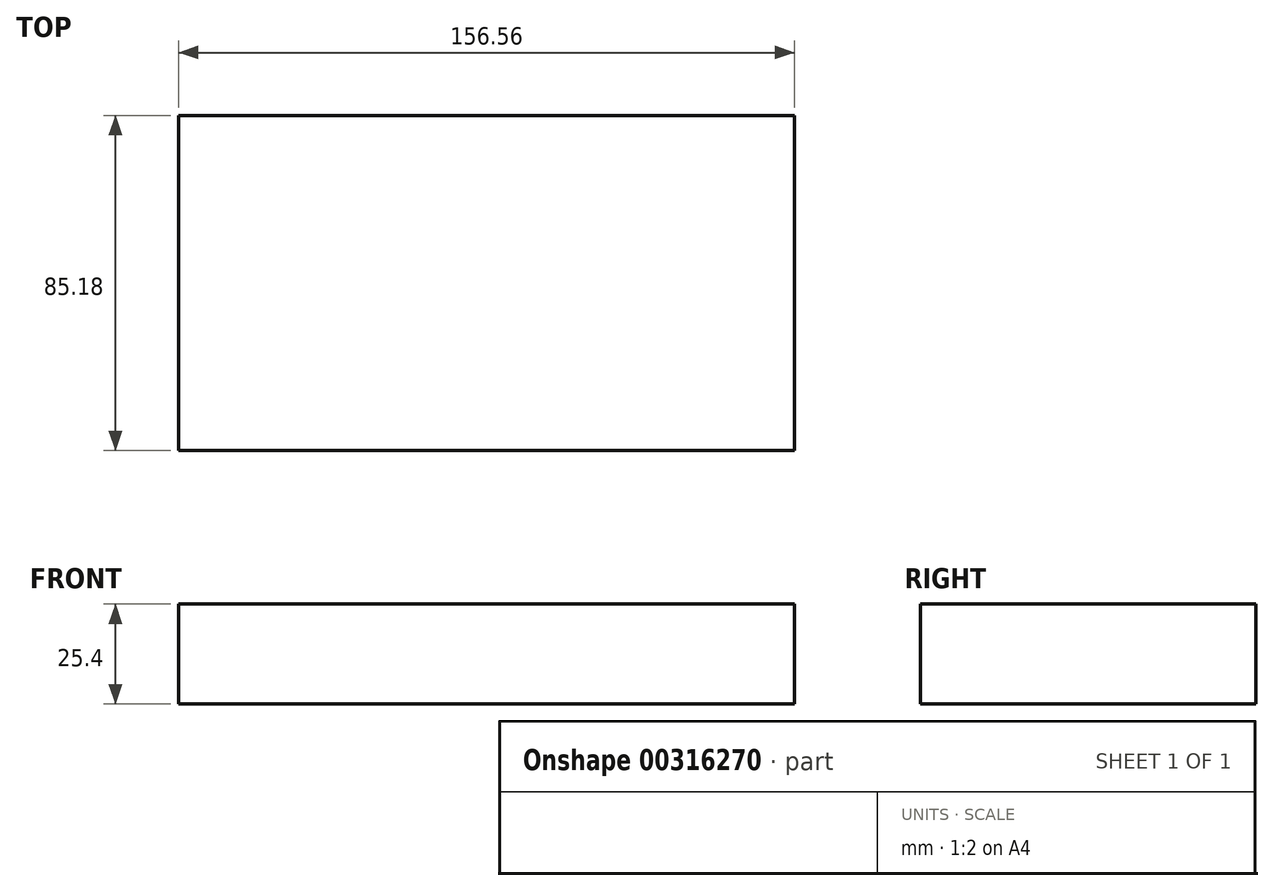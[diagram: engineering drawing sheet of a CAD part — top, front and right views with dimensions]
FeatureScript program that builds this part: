
annotation { "Feature Type Name" : "Feature", "Feature Type Description" : "" }
export const myFeature = defineFeature(function(context is Context, id is Id, definition is map)
    precondition{}
    {
        {
            var Q0;
            Q0=qCreatedBy(makeId("Top.planeOp"),FACE);
            var sketch = newSketch(context, id + "F0", { "sketchPlane" : qUnion([Q0])});
            skLineSegment(sketch, "E0.bottom", {"start": v(-124.66, 52.56) * mm, "end": v(31.9, 52.56) * mm});
            skLineSegment(sketch, "E0.top", {"start": v(-124.66, -32.62) * mm, "end": v(31.9, -32.62) * mm});
            skLineSegment(sketch, "E0.left", {"start": v(-124.66, 52.56) * mm, "end": v(-124.66, -32.62) * mm});
            skLineSegment(sketch, "E0.right", {"start": v(31.9, 52.56) * mm, "end": v(31.9, -32.62) * mm});
            skSolve(sketch);
        }
        {
            var Q0;
            Q0 = qSketchRegion(id + "F0", true);
            extrude(context, id + "F1", {"entities" : qUnion([Q0]), "oppositeDirection" : true, "depth" : 25.4 * mm});
        }
    });
